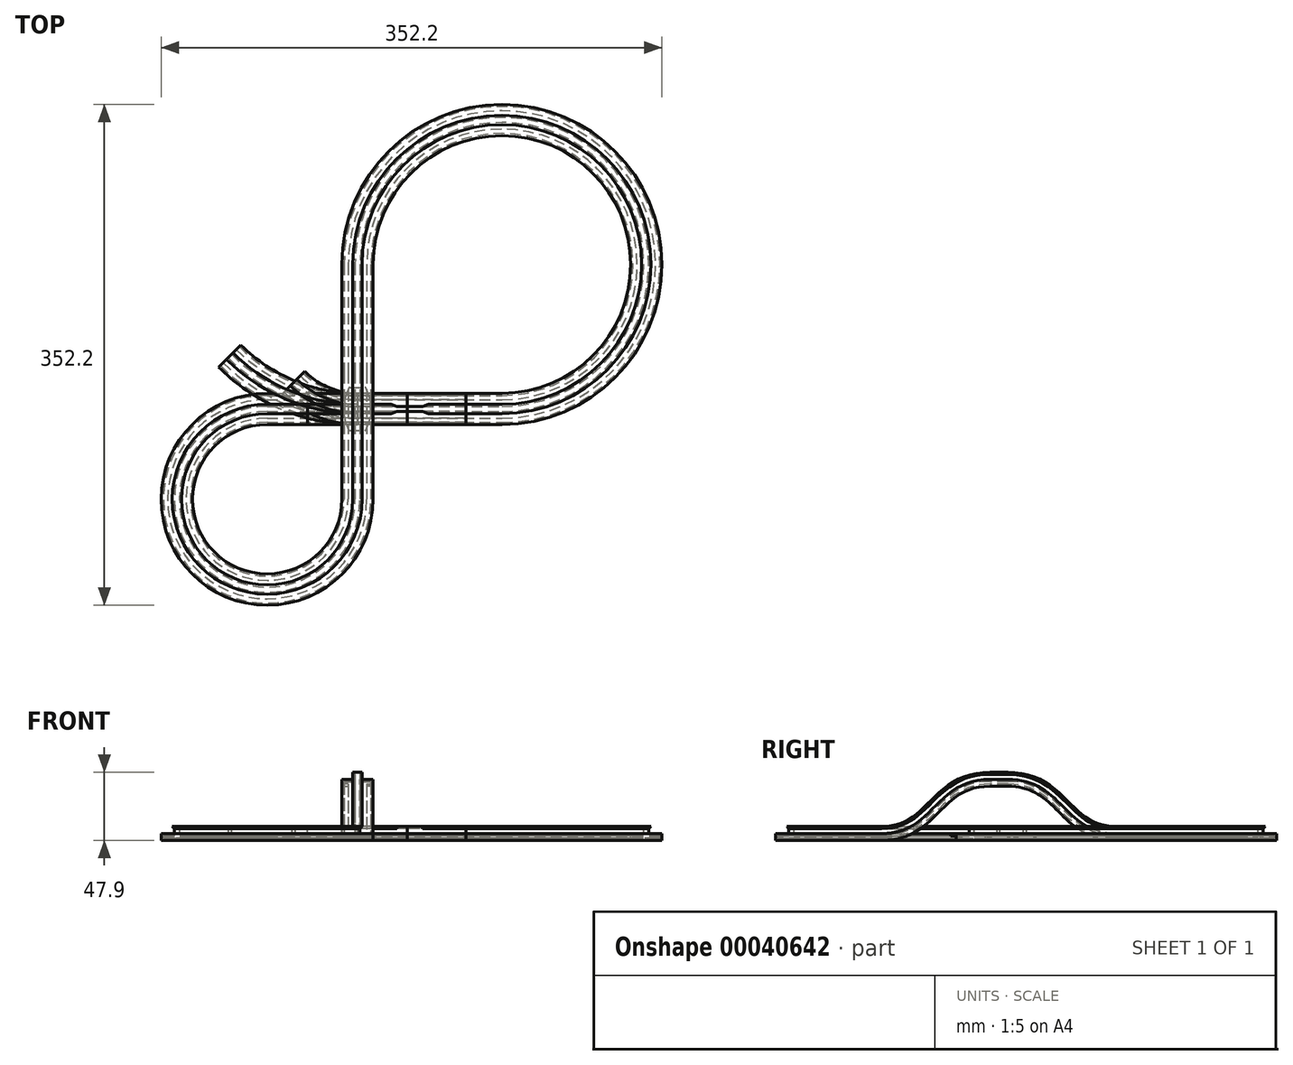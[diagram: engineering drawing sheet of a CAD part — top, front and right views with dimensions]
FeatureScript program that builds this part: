
annotation { "Feature Type Name" : "Feature", "Feature Type Description" : "" }
export const myFeature = defineFeature(function(context is Context, id is Id, definition is map)
    precondition{}
    {
        {
            var Q0;
            Q0=qCreatedBy(makeId("Top.planeOp"),FACE);
            var sketch = newSketch(context, id + "F0", { "sketchPlane" : qUnion([Q0])});
            skArc(sketch, "E0", {"start": v(101.6, 0) * mm, "mid": v(173.44, 173.44) * mm, "end": v(0, 101.6) * mm});
            skArc(sketch, "E1", {"start": v(-63.5, 0) * mm, "mid": v(-108.4, -108.4) * mm, "end": v(0, -63.5) * mm});
            skLineSegment(sketch, "E2", {"start": v(-63.5, 0) * mm, "end": v(0, 0) * mm});
            skLineSegment(sketch, "E3", {"start": v(0, 0) * mm, "end": v(101.6, 0) * mm});
            skSolve(sketch);
        }
        {
            var Q0;
            Q0=qCreatedBy(makeId("Right.planeOp"),FACE);
            var sketch = newSketch(context, id + "F1", { "sketchPlane" : qUnion([Q0])});
            skLineSegment(sketch, "E4", {"start": v(12.7, 38.1) * mm, "end": v(25.4, 38.1) * mm});
            skFitSpline(sketch, "E5", {"points": [v(-63.5, 0) * mm, v(12.7, 38.1) * mm], "startDerivative": vector(114.3, 0) * mm, "endDerivative": vector(114.3, 0) * mm});
            skFitSpline(sketch, "E6", {"points": [v(25.4, 38.1) * mm, v(101.6, 0) * mm], "startDerivative": vector(114.3, 0) * mm, "endDerivative": vector(114.3, 0) * mm});
            skSolve(sketch);
        }
        {
            var Q0;
            Q0=qCreatedBy(makeId("Right.planeOp"),FACE);
            var sketch = newSketch(context, id + "F2", { "sketchPlane" : qUnion([Q0])});
            skLineSegment(sketch, "E7", {"start": v(-11, 0) * mm, "end": v(11, 0) * mm});
            skLineSegment(sketch, "E8", {"start": v(11, 0) * mm, "end": v(11, 1.5) * mm});
            skLineSegment(sketch, "E9", {"start": v(11, 1.5) * mm, "end": v(1.75, 1.5) * mm});
            skLineSegment(sketch, "E10", {"start": v(1.75, 1.5) * mm, "end": v(1.75, 5) * mm});
            skLineSegment(sketch, "E11", {"start": v(1.75, 5) * mm, "end": v(3.25, 6.5) * mm});
            skLineSegment(sketch, "E12", {"start": v(3.25, 6.5) * mm, "end": v(-3.25, 6.5) * mm});
            skLineSegment(sketch, "E13", {"start": v(-3.25, 6.5) * mm, "end": v(-1.75, 5) * mm});
            skLineSegment(sketch, "E14", {"start": v(-1.75, 5) * mm, "end": v(-1.75, 1.5) * mm});
            skLineSegment(sketch, "E15", {"start": v(-1.75, 1.5) * mm, "end": v(-11, 1.5) * mm});
            skLineSegment(sketch, "E16", {"start": v(-11, 1.5) * mm, "end": v(-11, 0) * mm});
            skPoint(sketch, "E17", {"position": v(0, 6.5) * mm});
            skLineSegment(sketch, "E18", {"start": v(-11, 0) * mm, "end": v(-11, -3.3) * mm});
            skLineSegment(sketch, "E19", {"start": v(-11, -3.3) * mm, "end": v(-6.5, -3.3) * mm});
            skLineSegment(sketch, "E20", {"start": v(-6.5, -3.3) * mm, "end": v(-6.5, -1.8) * mm});
            skLineSegment(sketch, "E21", {"start": v(-6.5, -1.8) * mm, "end": v(-9.5, -1.8) * mm});
            skLineSegment(sketch, "E22", {"start": v(-9.5, -1.8) * mm, "end": v(-9.5, 0) * mm});
            skLineSegment(sketch, "E23", {"start": v(11, 0) * mm, "end": v(11, -3.3) * mm});
            skLineSegment(sketch, "E24", {"start": v(11, -3.3) * mm, "end": v(6.5, -3.3) * mm});
            skLineSegment(sketch, "E25", {"start": v(6.5, -3.3) * mm, "end": v(6.5, -1.8) * mm});
            skLineSegment(sketch, "E26", {"start": v(6.5, -1.8) * mm, "end": v(9.5, -1.8) * mm});
            skLineSegment(sketch, "E27", {"start": v(9.5, -1.8) * mm, "end": v(9.5, 0) * mm});
            skSolve(sketch);
        }
        {
            var Q0;
            Q0=qSketchRegion(id+"F2",true);
            var Q1;
            Q1=sQuery(id+"F0.wireOp",EDGE,"E3");
            var Q2;
            Q2=sQuery(id+"F0.wireOp",EDGE,"E0");
            var Q3;
            Q3=sQuery(id+"F1.wireOp",EDGE,"E6");
            var Q4;
            Q4=sQuery(id+"F1.wireOp",EDGE,"E4");
            var Q5;
            Q5=sQuery(id+"F1.wireOp",EDGE,"E5");
            var Q6;
            Q6=sQuery(id+"F0.wireOp",EDGE,"E1");
            var Q7;
            Q7=sQuery(id+"F0.wireOp",EDGE,"E2");
            sweep(context, id + "F3", {"profiles" : qUnion([Q0]), "path" : qUnion([Q1, Q2, Q3, Q4, Q5, Q6, Q7])});
        }
        {
            var Q0;
            Q0=qSketchRegion(id+"F2",true);
            extrude(context, id + "F4", {"entities" : qUnion([Q0]), "endBound" : BoundingType.SYMMETRIC, "depth" : 70 * mm});
        }
        {
            var Q0;
            Q0=makeQuery(id+"F3.opSweep","SWEPT_FACE",FACE,{"disambiguationData":[OSD([sQuery(id+"F0.wireOp",EDGE,"E2"),sQuery(id+"F2.wireOp",EDGE,"E12")])]});
            var sketch = newSketch(context, id + "F5", { "sketchPlane" : qUnion([Q0])});
            skLineSegment(sketch, "E28", {"start": v(50, 3.25) * mm, "end": v(50, -3.25) * mm});
            skLineSegment(sketch, "E29", {"start": v(50, -3.25) * mm, "end": v(45.87, -1.75) * mm});
            skLineSegment(sketch, "E30", {"start": v(45.87, -1.75) * mm, "end": v(27.87, -1.75) * mm});
            skLineSegment(sketch, "E31", {"start": v(27.87, -1.75) * mm, "end": v(23.75, -3.25) * mm});
            skLineSegment(sketch, "E32", {"start": v(23.75, -3.25) * mm, "end": v(23.75, 3.25) * mm});
            skLineSegment(sketch, "E33", {"start": v(23.75, 3.25) * mm, "end": v(27.87, 1.75) * mm});
            skLineSegment(sketch, "E34", {"start": v(27.87, 1.75) * mm, "end": v(45.87, 1.75) * mm});
            skLineSegment(sketch, "E35", {"start": v(45.87, 1.75) * mm, "end": v(50, 3.25) * mm});
            skLineSegment(sketch, "E36", {"start": v(50, 3.25) * mm, "end": v(23.75, 3.25) * mm});
            skLineSegment(sketch, "E37", {"start": v(50, -3.25) * mm, "end": v(23.75, -3.25) * mm});
            skSolve(sketch);
        }
        {
            var Q0;
            Q0=makeQuery(id+"F5.imprint","IMPRINT",FACE,{"disambiguationData":[TD([[makeQuery(id+"F5.imprint","IMPRINT",EDGE,{"derivedFrom":sQuery(id+"F5.wireOp",EDGE,"E33")}),1.0]])]});
            var Q1;
            Q1=makeQuery(id+"F5.imprint","IMPRINT",FACE,{"disambiguationData":[TD([[makeQuery(id+"F5.imprint","IMPRINT",EDGE,{"derivedFrom":sQuery(id+"F5.wireOp",EDGE,"E29")}),1.0]])]});
            extrude(context, id + "F6", {"entities" : qUnion([Q0, Q1]), "operationType" : NewBodyOperationType.REMOVE, "oppositeDirection" : true, "depth" : 1.5 * mm});
        }
        {
            var Q0;
            Q0=qCreatedBy(makeId("Top.planeOp"),FACE);
            var sketch = newSketch(context, id + "F7", { "sketchPlane" : qUnion([Q0])});
            skArc(sketch, "E38", {"start": v(-44.9, 18.6) * mm, "mid": v(-24.3, 4.83) * mm, "end": v(0, 0) * mm});
            skLineSegment(sketch, "E39", {"start": v(0, 63.5) * mm, "end": v(-44.9, 18.6) * mm, "construction": true});
            skSolve(sketch);
        }
        {
            var Q0;
            Q0=qSketchRegion(id+"F2",true);
            var Q1;
            Q1=sQuery(id+"F7.wireOp",EDGE,"E38");
            sweep(context, id + "F8", {"profiles" : qUnion([Q0]), "path" : qUnion([Q1])});
        }
        {
            var Q0;
            Q0=qCreatedBy(makeId("Top.planeOp"),FACE);
            var sketch = newSketch(context, id + "F9", { "sketchPlane" : qUnion([Q0])});
            skLineSegment(sketch, "E40.bottom", {"start": v(-5.3, 15) * mm, "end": v(5.3, 15) * mm});
            skLineSegment(sketch, "E40.top", {"start": v(-5.3, -15) * mm, "end": v(5.3, -15) * mm});
            skLineSegment(sketch, "E40.left", {"start": v(-9, 6.05) * mm, "end": v(-9, -6.05) * mm});
            skLineSegment(sketch, "E40.right", {"start": v(9, 6.05) * mm, "end": v(9, -6.05) * mm});
            skPoint(sketch, "E41", {"position": v(0, 15) * mm});
            skPoint(sketch, "E42", {"position": v(9, 0) * mm});
            skLineSegment(sketch, "E43", {"start": v(-6.24, 14.34) * mm, "end": v(-8.76, 7.42) * mm});
            skPoint(sketch, "E44.orphan", {"position": v(-9, 15) * mm});
            skLineSegment(sketch, "E45", {"start": v(-6.24, -14.34) * mm, "end": v(-8.76, -7.42) * mm});
            skLineSegment(sketch, "E46", {"start": v(8.76, 7.42) * mm, "end": v(6.24, 14.34) * mm});
            skLineSegment(sketch, "E47", {"start": v(6.24, -14.34) * mm, "end": v(8.76, -7.42) * mm});
            skPoint(sketch, "E48.orphan", {"position": v(9, 15) * mm});
            skPoint(sketch, "E49.orphan", {"position": v(9, -15) * mm});
            skPoint(sketch, "E50.visualSharp", {"position": v(-6, 15) * mm});
            skArc(sketch, "E50.filletArc", {"start": v(-5.3, 15) * mm, "mid": v(-5.87, 14.82) * mm, "end": v(-6.24, 14.34) * mm});
            skPoint(sketch, "E51.visualSharp", {"position": v(6, 15) * mm});
            skArc(sketch, "E51.filletArc", {"start": v(6.24, 14.34) * mm, "mid": v(5.87, 14.82) * mm, "end": v(5.3, 15) * mm});
            skPoint(sketch, "E52.visualSharp", {"position": v(6, -15) * mm});
            skArc(sketch, "E52.filletArc", {"start": v(5.3, -15) * mm, "mid": v(5.87, -14.82) * mm, "end": v(6.24, -14.34) * mm});
            skPoint(sketch, "E53.visualSharp", {"position": v(-6, -15) * mm});
            skArc(sketch, "E53.filletArc", {"start": v(-6.24, -14.34) * mm, "mid": v(-5.87, -14.82) * mm, "end": v(-5.3, -15) * mm});
            skPoint(sketch, "E54.visualSharp", {"position": v(-9, -6.76) * mm});
            skArc(sketch, "E54.filletArc", {"start": v(-9, -6.05) * mm, "mid": v(-8.94, -6.75) * mm, "end": v(-8.76, -7.42) * mm});
            skPoint(sketch, "E55.visualSharp", {"position": v(9, -6.76) * mm});
            skArc(sketch, "E55.filletArc", {"start": v(8.76, -7.42) * mm, "mid": v(8.94, -6.75) * mm, "end": v(9, -6.05) * mm});
            skPoint(sketch, "E56.visualSharp", {"position": v(9, 6.76) * mm});
            skArc(sketch, "E56.filletArc", {"start": v(9, 6.05) * mm, "mid": v(8.94, 6.75) * mm, "end": v(8.76, 7.42) * mm});
            skPoint(sketch, "E57.visualSharp", {"position": v(-9, 6.76) * mm});
            skArc(sketch, "E57.filletArc", {"start": v(-8.76, 7.42) * mm, "mid": v(-8.94, 6.75) * mm, "end": v(-9, 6.05) * mm});
            skSolve(sketch);
        }
        {
            var Q0;
            Q0=qSketchRegion(id+"F9",true);
            extrude(context, id + "F10", {"entities" : qUnion([Q0]), "depth" : 1.25 * mm});
        }
        {
            var Q0;
            Q0=qCreatedBy(makeId("Top.planeOp"),FACE);
            var sketch = newSketch(context, id + "F11", { "sketchPlane" : qUnion([Q0])});
            skArc(sketch, "E58", {"start": v(-89.8, 37.2) * mm, "mid": v(-48.6, 9.67) * mm, "end": v(0, 0) * mm});
            skLineSegment(sketch, "E59", {"start": v(-89.8, 37.2) * mm, "end": v(0, 127) * mm, "construction": true});
            skSolve(sketch);
        }
        {
            var Q0;
            Q0=qSketchRegion(id+"F2",true);
            var Q1;
            Q1=sQuery(id+"F11.wireOp",EDGE,"E58");
            sweep(context, id + "F12", {"profiles" : qUnion([Q0]), "path" : qUnion([Q1])});
        }
        {
            var Q0;
            Q0=qSketchRegion(id+"F2",true);
            extrude(context, id + "F13", {"entities" : qUnion([Q0]), "depth" : 76.2 * mm});
        }
        {
            var Q0;
            Q0=makeQuery(id+"F13.opExtrude","SWEPT_BODY",BODY,{"disambiguationData":[OSD([sQuery(id+"F2.wireOp",EDGE,"E7"),sQuery(id+"F2.wireOp",EDGE,"E8"),sQuery(id+"F2.wireOp",EDGE,"E9"),sQuery(id+"F2.wireOp",EDGE,"E10"),sQuery(id+"F2.wireOp",EDGE,"E11"),sQuery(id+"F2.wireOp",EDGE,"88f99a0e-11cf-46aa-87f3-ce1f019fea90"),sQuery(id+"F2.wireOp",EDGE,"E12"),sQuery(id+"F2.wireOp",EDGE,"E13"),sQuery(id+"F2.wireOp",EDGE,"3d854aa4-51c6-49de-bb36-199323c5fd28"),sQuery(id+"F2.wireOp",EDGE,"E14"),sQuery(id+"F2.wireOp",EDGE,"E15"),sQuery(id+"F2.wireOp",EDGE,"E16"),sQuery(id+"F2.wireOp",EDGE,"E18"),sQuery(id+"F2.wireOp",EDGE,"E19"),sQuery(id+"F2.wireOp",EDGE,"E20"),sQuery(id+"F2.wireOp",EDGE,"E21"),sQuery(id+"F2.wireOp",EDGE,"E22"),sQuery(id+"F2.wireOp",EDGE,"E23"),sQuery(id+"F2.wireOp",EDGE,"E24"),sQuery(id+"F2.wireOp",EDGE,"E25"),sQuery(id+"F2.wireOp",EDGE,"E26"),sQuery(id+"F2.wireOp",EDGE,"E27")])]});
            transform(context, id + "F14", {"entities" : qUnion([Q0]), "transformType" : TransformType.TRANSLATION_3D, "dx" : 0 * mm, "dy" : 0 * mm, "dz" : 0 * mm, "makeCopy" : true});
        }
        {
            var Q0;
            Q0=makeQuery(id+"F5.imprint","IMPRINT",FACE,{"disambiguationData":[TD([[makeQuery(id+"F5.imprint","IMPRINT",EDGE,{"derivedFrom":sQuery(id+"F5.wireOp",EDGE,"E33")}),1.0]])]});
            var Q1;
            Q1=makeQuery(id+"F5.imprint","IMPRINT",FACE,{"disambiguationData":[TD([[makeQuery(id+"F5.imprint","IMPRINT",EDGE,{"derivedFrom":sQuery(id+"F5.wireOp",EDGE,"E29")}),1.0]])]});
            extrude(context, id + "F15", {"entities" : qUnion([Q0, Q1]), "operationType" : NewBodyOperationType.REMOVE, "oppositeDirection" : true, "depth" : 1.5 * mm});
        }
    });
